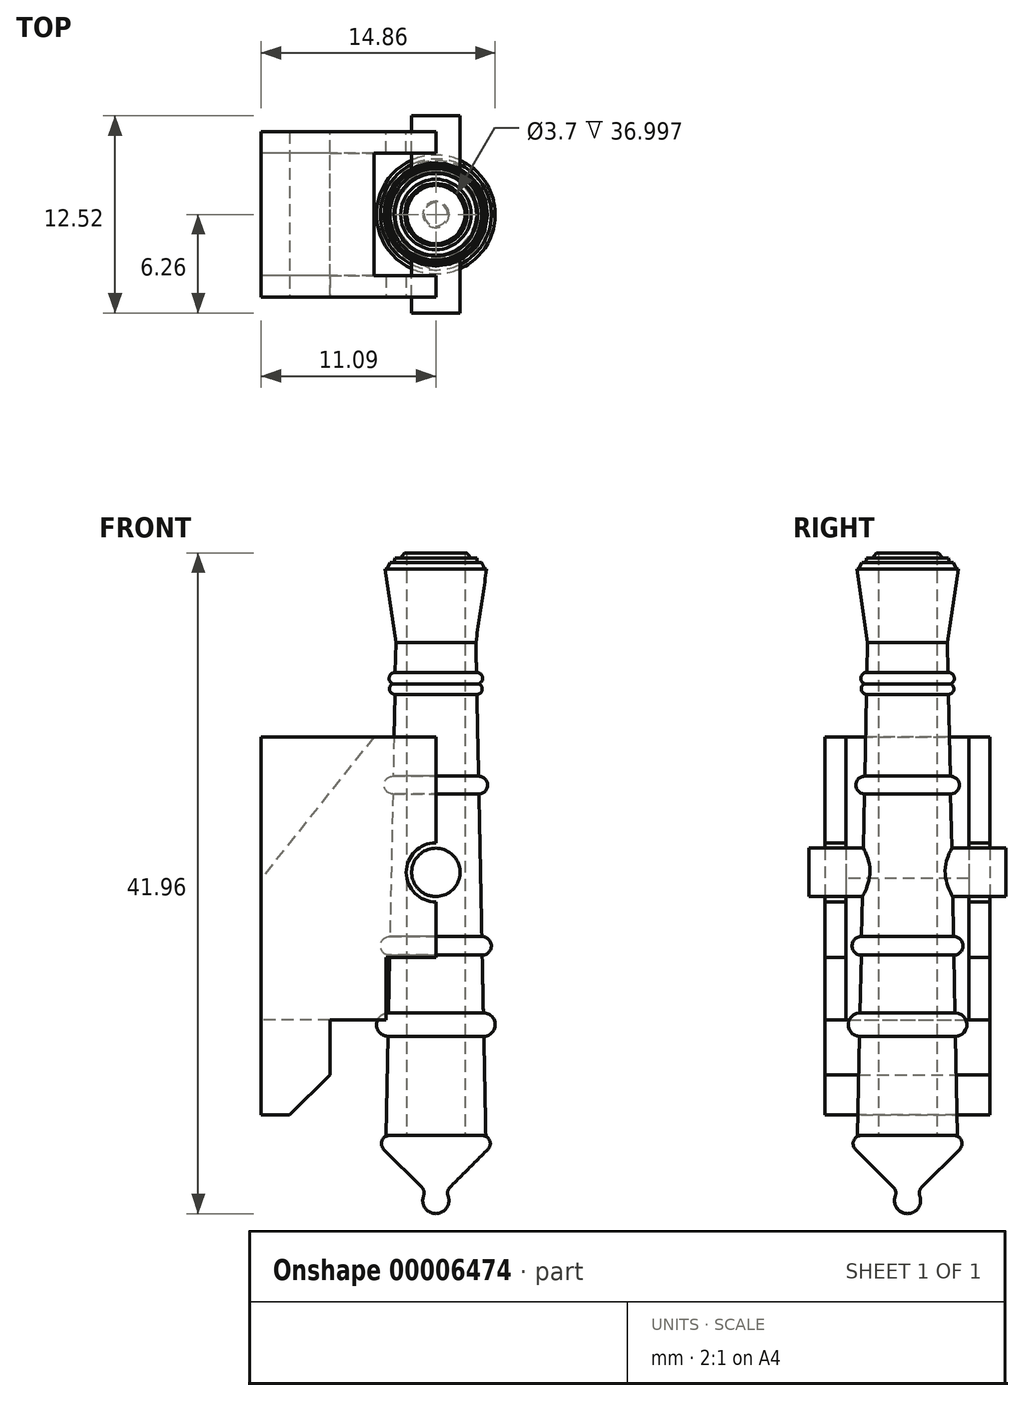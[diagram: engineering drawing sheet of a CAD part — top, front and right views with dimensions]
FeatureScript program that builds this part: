
annotation { "Feature Type Name" : "Feature", "Feature Type Description" : "" }
export const myFeature = defineFeature(function(context is Context, id is Id, definition is map)
    precondition{}
    {
        {
            var Q0;
            Q0=qCreatedBy(makeId("Front.planeOp"),FACE);
            var sketch = newSketch(context, id + "F0", { "sketchPlane" : qUnion([Q0])});
            skLineSegment(sketch, "E0", {"start": v(0, 31.33) * mm, "end": v(0, -18.28) * mm, "construction": true});
            skLineSegment(sketch, "E1", {"start": v(0, 0) * mm, "end": v(3.18, 0) * mm});
            skLineSegment(sketch, "E2", {"start": v(3.18, 0) * mm, "end": v(3.05, 6.3) * mm});
            skLineSegment(sketch, "E3", {"start": v(2.54, 31.33) * mm, "end": v(3.23, 35.97) * mm});
            skLineSegment(sketch, "E4", {"start": v(3.23, 35.97) * mm, "end": v(3.1, 35.97) * mm});
            skLineSegment(sketch, "E5", {"start": v(0, 35.97) * mm, "end": v(0, 0) * mm});
            skArc(sketch, "E6", {"start": v(2.45, 28.69) * mm, "mid": v(2.73, 29.4) * mm, "end": v(2.45, 28.69) * mm});
            skArc(sketch, "E7", {"start": v(2.45, 28.69) * mm, "mid": v(2.75, 28.06) * mm, "end": v(2.45, 28.69) * mm});
            skArc(sketch, "E8", {"start": v(2.74, 21.7) * mm, "mid": v(3.29, 22.27) * mm, "end": v(2.71, 22.83) * mm});
            skArc(sketch, "E9", {"start": v(2.94, 11.46) * mm, "mid": v(3.53, 12.07) * mm, "end": v(2.92, 12.65) * mm});
            skArc(sketch, "E10", {"start": v(3.05, 6.3) * mm, "mid": v(3.77, 7.06) * mm, "end": v(3.02, 7.78) * mm});
            skLineSegment(sketch, "E11.trimOffspring", {"start": v(3.02, 7.78) * mm, "end": v(2.94, 11.46) * mm});
            skLineSegment(sketch, "E12.trimOffspring", {"start": v(2.92, 12.65) * mm, "end": v(2.74, 21.7) * mm});
            skLineSegment(sketch, "E13.trimOffspring", {"start": v(2.71, 22.83) * mm, "end": v(2.6, 28.03) * mm});
            skLineSegment(sketch, "E14.trimOffspring", {"start": v(2.58, 29.42) * mm, "end": v(2.54, 31.33) * mm});
            skArc(sketch, "E15.trimOffspring", {"start": v(2.74, 28.7) * mm, "mid": v(2.96, 29.12) * mm, "end": v(2.58, 29.42) * mm});
            skArc(sketch, "E16.trimOffspring", {"start": v(2.6, 28.03) * mm, "mid": v(2.94, 28.3) * mm, "end": v(2.74, 28.7) * mm});
            skLineSegment(sketch, "E17", {"start": v(3.1, 35.97) * mm, "end": v(2.91, 36.4) * mm});
            skLineSegment(sketch, "E18", {"start": v(2.91, 36.4) * mm, "end": v(2.65, 36.4) * mm});
            skLineSegment(sketch, "E19", {"start": v(2.65, 36.4) * mm, "end": v(2.6, 36.69) * mm});
            skLineSegment(sketch, "E20", {"start": v(2.6, 36.69) * mm, "end": v(2.24, 36.69) * mm});
            skLineSegment(sketch, "E21", {"start": v(2.24, 36.69) * mm, "end": v(1.98, 37) * mm});
            skLineSegment(sketch, "E22", {"start": v(1.98, 37) * mm, "end": v(0, 37) * mm});
            skLineSegment(sketch, "E23", {"start": v(0, 37) * mm, "end": v(0, 35.97) * mm});
            skSolve(sketch);
        }
        {
            var Q0;
            Q0=makeQuery(id+"F0.imprint","IMPRINT",FACE,{"disambiguationData":[TD([[makeQuery(id+"F0.imprint","IMPRINT",EDGE,{"derivedFrom":sQuery(id+"F0.wireOp",EDGE,"E1")}),1.0]])]});
            var Q1;
            Q1=sQuery(id+"F0.wireOp",EDGE,"E5");
            revolve(context, id + "F1", {"entities" : qUnion([Q0]), "axis" : qUnion([Q1]), "revolveType" : RevolveType.FULL});
        }
        {
            var Q0;
            Q0=qCreatedBy(makeId("Right.planeOp"),FACE);
            var sketch = newSketch(context, id + "F2", { "sketchPlane" : qUnion([Q0])});
            skLineSegment(sketch, "E24", {"start": v(0, 0) * mm, "end": v(-4.18, 0) * mm});
            skArc(sketch, "E25", {"start": v(-0.61, -3.57) * mm, "mid": v(-0.76, -4.46) * mm, "end": v(0, -4.96) * mm});
            skLineSegment(sketch, "E26", {"start": v(-4.18, 0) * mm, "end": v(-0.61, -3.57) * mm});
            skLineSegment(sketch, "E27", {"start": v(0, 0) * mm, "end": v(0, -4.96) * mm});
            skSolve(sketch);
        }
        {
            var Q0;
            Q0=makeQuery(id+"F2.imprint","IMPRINT",FACE,{"disambiguationData":[TD([[makeQuery(id+"F2.imprint","IMPRINT",EDGE,{"derivedFrom":sQuery(id+"F2.wireOp",EDGE,"E24")}),1.0]])]});
            var Q1;
            Q1=sQuery(id+"F2.wireOp",EDGE,"E27");
            revolve(context, id + "F3", {"entities" : qUnion([Q0]), "axis" : qUnion([Q1]), "revolveType" : RevolveType.FULL});
        }
        {
            var Q0;
            Q0=makeQuery(id+"F3.opRevolve","SWEPT_EDGE",EDGE,{"disambiguationData":[OSD([sQuery(id+"F2.wireOp",EDGE,"E25"),sQuery(id+"F2.wireOp",EDGE,"E26")])]});
            var Q1;
            Q1=makeQuery(id+"F3.opRevolve","SWEPT_EDGE",EDGE,{"disambiguationData":[OSD([sQuery(id+"F2.wireOp",EDGE,"E24"),sQuery(id+"F2.wireOp",EDGE,"E26")])]});
            fillet(context, id + "F4", {"entities" : qUnion([Q0, Q1]), "radius" : 0.5 * mm, "tangentPropagation" : true, "allowEdgeOverflow" : false});
        }
        {
            var Q0;
            Q0=qCreatedBy(makeId("Front.planeOp"),FACE);
            var sketch = newSketch(context, id + "F5", { "sketchPlane" : qUnion([Q0])});
            skLineSegment(sketch, "E28", {"start": v(0, -11.6) * mm, "end": v(0, 39.68) * mm, "construction": true});
            skCircle(sketch, "E29", {"center": v(0, 16.72) * mm, "radius": 1.54 * mm});
            skSolve(sketch);
        }
        {
            var Q0;
            Q0 = qSketchRegion(id + "F5", true);
            extrude(context, id + "F6", {"entities" : qUnion([Q0]), "operationType" : NewBodyOperationType.ADD, "endBound" : BoundingType.SYMMETRIC, "depth" : 12.52 * mm});
        }
        {
            var Q0;
            Q0=makeQuery(id+"F6.opExtrude","CAP_FACE",FACE,{"disambiguationData":[OSD([sQuery(id+"F5.wireOp",EDGE,"E29")])],"isStart":false});
            cPlane(context, id + "F7", {"entities" : qUnion([Q0]), "cplaneType" : CPlaneType.OFFSET, "offset" : 1.02 * mm, "oppositeDirection" : true, "width" : 152.4 * mm, "height" : 152.4 * mm});
        }
        {
            var Q0;
            Q0=qCreatedBy(id+"F7.planeOp",FACE);
            var sketch = newSketch(context, id + "F8", { "sketchPlane" : qUnion([Q0])});
            skCircle(sketch, "E30.0", {"center": v(0, 16.72) * mm, "radius": 1.54 * mm, "construction": true});
            skArc(sketch, "E31", {"start": v(0, 18.6) * mm, "mid": v(-1.88, 16.72) * mm, "end": v(0, 14.84) * mm});
            skLineSegment(sketch, "E32", {"start": v(0, 18.6) * mm, "end": v(0, 25.32) * mm});
            skLineSegment(sketch, "E33", {"start": v(0, 25.32) * mm, "end": v(-11.1, 25.32) * mm});
            skLineSegment(sketch, "E34", {"start": v(-11.1, 25.32) * mm, "end": v(-11.1, 1.33) * mm});
            skLineSegment(sketch, "E35", {"start": v(-11.1, 1.33) * mm, "end": v(-6.74, 1.33) * mm});
            skLineSegment(sketch, "E36", {"start": v(-6.74, 1.33) * mm, "end": v(-6.74, 7.35) * mm});
            skLineSegment(sketch, "E37", {"start": v(-6.74, 7.35) * mm, "end": v(-3.17, 7.35) * mm});
            skLineSegment(sketch, "E38", {"start": v(-3.17, 7.35) * mm, "end": v(-3.17, 11.3) * mm});
            skLineSegment(sketch, "E39", {"start": v(-3.17, 11.3) * mm, "end": v(0, 11.3) * mm});
            skLineSegment(sketch, "E40", {"start": v(0, 11.3) * mm, "end": v(0, 14.84) * mm});
            skSolve(sketch);
        }
        {
            var Q0;
            Q0=makeQuery(id+"F8.imprint","IMPRINT",FACE,{"disambiguationData":[TD([[makeQuery(id+"F8.imprint","IMPRINT",EDGE,{"derivedFrom":sQuery(id+"F8.wireOp",EDGE,"E31")}),-1.0]])]});
            extrude(context, id + "F9", {"entities" : qUnion([Q0]), "oppositeDirection" : true, "depth" : 1.34 * mm});
        }
        {
            var Q0;
            Q0=makeQuery(id+"F9.opExtrude","SWEPT_BODY",BODY,{"disambiguationData":[OSD([sQuery(id+"F8.wireOp",EDGE,"E31"),sQuery(id+"F8.wireOp",EDGE,"E32"),sQuery(id+"F8.wireOp",EDGE,"E33"),sQuery(id+"F8.wireOp",EDGE,"E34"),sQuery(id+"F8.wireOp",EDGE,"E35"),sQuery(id+"F8.wireOp",EDGE,"E36"),sQuery(id+"F8.wireOp",EDGE,"E37"),sQuery(id+"F8.wireOp",EDGE,"E38"),sQuery(id+"F8.wireOp",EDGE,"E39"),sQuery(id+"F8.wireOp",EDGE,"E40")])]});
            var Q1;
            Q1=qCreatedBy(makeId("Front.planeOp"),FACE);
            mirror(context, id + "F10", {"entities" : qUnion([Q0]), "mirrorPlane" : qUnion([Q1])});
        }
        {
            var Q0;
            Q0=makeQuery(id+"F10.opPattern","COPY",FACE,{"derivedFrom":makeQuery(id+"F9.opExtrude","CAP_FACE",FACE,{"disambiguationData":[OSD([sQuery(id+"F8.wireOp",EDGE,"E31"),sQuery(id+"F8.wireOp",EDGE,"E32"),sQuery(id+"F8.wireOp",EDGE,"E33"),sQuery(id+"F8.wireOp",EDGE,"E34"),sQuery(id+"F8.wireOp",EDGE,"E35"),sQuery(id+"F8.wireOp",EDGE,"E36"),sQuery(id+"F8.wireOp",EDGE,"E37"),sQuery(id+"F8.wireOp",EDGE,"E38"),sQuery(id+"F8.wireOp",EDGE,"E39"),sQuery(id+"F8.wireOp",EDGE,"E40")])],"isStart":false}),"instanceName":"1"});
            var sketch = newSketch(context, id + "F11", { "sketchPlane" : qUnion([Q0])});
            skLineSegment(sketch, "E41.0", {"start": v(-6.74, 1.33) * mm, "end": v(-6.74, 7.35) * mm});
            skLineSegment(sketch, "E41.1", {"start": v(-11.1, 1.33) * mm, "end": v(-6.74, 1.33) * mm});
            skLineSegment(sketch, "E42", {"start": v(-6.74, 7.35) * mm, "end": v(-11.1, 7.35) * mm});
            skLineSegment(sketch, "E43", {"start": v(-11.1, 7.35) * mm, "end": v(-11.1, 1.33) * mm});
            skSolve(sketch);
        }
        {
            var Q0;
            Q0=makeQuery(id+"F11.imprint","IMPRINT",FACE,{"disambiguationData":[TD([[makeQuery(id+"F11.imprint","IMPRINT",EDGE,{"derivedFrom":sQuery(id+"F11.wireOp",EDGE,"E41.0")}),1.0]])]});
            extrude(context, id + "F12", {"entities" : qUnion([Q0]), "endBound" : BoundingType.UP_TO_NEXT, "depth" : 25.4 * mm});
        }
        {
            var Q0;
            Q0=makeQuery(id+"F10.opPattern","COPY",BODY,{"derivedFrom":makeQuery(id+"F9.opExtrude","SWEPT_BODY",BODY,{"disambiguationData":[OSD([sQuery(id+"F8.wireOp",EDGE,"E31"),sQuery(id+"F8.wireOp",EDGE,"E32"),sQuery(id+"F8.wireOp",EDGE,"E33"),sQuery(id+"F8.wireOp",EDGE,"E34"),sQuery(id+"F8.wireOp",EDGE,"E35"),sQuery(id+"F8.wireOp",EDGE,"E36"),sQuery(id+"F8.wireOp",EDGE,"E37"),sQuery(id+"F8.wireOp",EDGE,"E38"),sQuery(id+"F8.wireOp",EDGE,"E39"),sQuery(id+"F8.wireOp",EDGE,"E40")])]}),"instanceName":"1"});
            var Q1;
            Q1=makeQuery(id+"F12.opExtrude","SWEPT_BODY",BODY,{"disambiguationData":[OSD([sQuery(id+"F11.wireOp",EDGE,"E41.0"),sQuery(id+"F11.wireOp",EDGE,"E41.1"),sQuery(id+"F11.wireOp",EDGE,"E42"),sQuery(id+"F11.wireOp",EDGE,"E43")])]});
            var Q2;
            Q2=makeQuery(id+"F9.opExtrude","SWEPT_BODY",BODY,{"disambiguationData":[OSD([sQuery(id+"F8.wireOp",EDGE,"E31"),sQuery(id+"F8.wireOp",EDGE,"E32"),sQuery(id+"F8.wireOp",EDGE,"E33"),sQuery(id+"F8.wireOp",EDGE,"E34"),sQuery(id+"F8.wireOp",EDGE,"E35"),sQuery(id+"F8.wireOp",EDGE,"E36"),sQuery(id+"F8.wireOp",EDGE,"E37"),sQuery(id+"F8.wireOp",EDGE,"E38"),sQuery(id+"F8.wireOp",EDGE,"E39"),sQuery(id+"F8.wireOp",EDGE,"E40")])]});
            booleanBodies(context, id + "F13", {"operationType" : BooleanOperationType.UNION, "tools" : qUnion([Q0, Q1, Q2])});
        }
        {
            var Q0;
            {var subQ0=makeQuery(id+"F9.opExtrude","SWEPT_EDGE",EDGE,{"disambiguationData":[OSD([sQuery(id+"F8.wireOp",EDGE,"E35"),sQuery(id+"F8.wireOp",EDGE,"E36")])]});Q0=makeQuery(id+"F13.opBoolean","MERGE",EDGE,{"derivedFrom":[subQ0,makeQuery(id+"F10.opPattern","COPY",EDGE,{"derivedFrom":subQ0,"instanceName":"1"}),makeQuery(id+"F12.opExtrude","SWEPT_EDGE",EDGE,{"disambiguationData":[OSD([sQuery(id+"F11.wireOp",EDGE,"E41.0"),sQuery(id+"F11.wireOp",EDGE,"E41.1")])]})]});}
            chamfer(context, id + "F14", {"entities" : qUnion([Q0]), "width" : 2.54 * mm, "tangentPropagation" : true});
        }
        {
            var Q0;
            Q0=makeQuery(id+"F9.opExtrude","CAP_FACE",FACE,{"disambiguationData":[OSD([sQuery(id+"F8.wireOp",EDGE,"E31"),sQuery(id+"F8.wireOp",EDGE,"E32"),sQuery(id+"F8.wireOp",EDGE,"E33"),sQuery(id+"F8.wireOp",EDGE,"E34"),sQuery(id+"F8.wireOp",EDGE,"E35"),sQuery(id+"F8.wireOp",EDGE,"E36"),sQuery(id+"F8.wireOp",EDGE,"E37"),sQuery(id+"F8.wireOp",EDGE,"E38"),sQuery(id+"F8.wireOp",EDGE,"E39"),sQuery(id+"F8.wireOp",EDGE,"E40")])],"isStart":false});
            var sketch = newSketch(context, id + "F15", { "sketchPlane" : qUnion([Q0])});
            skLineSegment(sketch, "E44.0", {"start": v(0, 25.32) * mm, "end": v(11.1, 25.32) * mm});
            skLineSegment(sketch, "E44.1", {"start": v(11.1, 25.32) * mm, "end": v(11.1, 7.35) * mm});
            skLineSegment(sketch, "E45", {"start": v(3.94, 25.32) * mm, "end": v(11.1, 16.33) * mm});
            skSolve(sketch);
        }
        {
            var Q0;
            {var subQ0=sQuery(id+"F15.wireOp",EDGE,"E45");Q0=makeQuery(id+"F15.imprint","IMPRINT",FACE,{"disambiguationData":[TD([[makeQuery(id+"F15.imprint","IMPRINT",EDGE,{"derivedFrom":subQ0}),1.0]])]});}
            extrude(context, id + "F16", {"entities" : qUnion([Q0]), "operationType" : NewBodyOperationType.ADD, "endBound" : BoundingType.UP_TO_NEXT, "depth" : 25.4 * mm});
        }
        {
            var Q0;
            Q0=makeQuery(id+"F1.opRevolve","SWEPT_FACE",FACE,{"disambiguationData":[OSD([sQuery(id+"F0.wireOp",EDGE,"E1")])]});
            var sketch = newSketch(context, id + "F17", { "sketchPlane" : qUnion([Q0])});
            skCircle(sketch, "E46", {"center": v(0, 0) * mm, "radius": 1.85 * mm});
            skSolve(sketch);
        }
        {
            var Q0;
            Q0=makeQuery(id+"F17.imprint","IMPRINT",FACE,{"disambiguationData":[TD([[makeQuery(id+"F17.imprint","IMPRINT",EDGE,{"derivedFrom":sQuery(id+"F17.wireOp",EDGE,"E46")}),1.0]])]});
            extrude(context, id + "F18", {"entities" : qUnion([Q0]), "operationType" : NewBodyOperationType.REMOVE, "endBound" : BoundingType.THROUGH_ALL, "oppositeDirection" : true, "depth" : 25.4 * mm});
        }
    });
